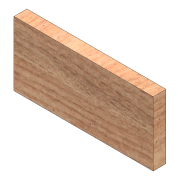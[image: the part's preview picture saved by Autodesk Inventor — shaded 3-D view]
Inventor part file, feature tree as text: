
AUTODESK INVENTOR PART (.ipt)
format: ipt  version: 2018 (Build 220112000, 112)  size: 108,032 bytes
history: native  units: mm
features: extrude x1, sketch x1
ambient origin geometry x8: Origin, YZ Plane, XZ Plane, XY Plane, X Axis, Y Axis, Z Axis, Center Point
bodies: Solid1 (feature_tree)
feature tree (2):
  extrude  "Extrusion1"  Depth=100.0mm
  sketch  "Sketch2"  dims[d0=215.668mm d1=100.0mm d2=20.0mm d3=0.0mm]
